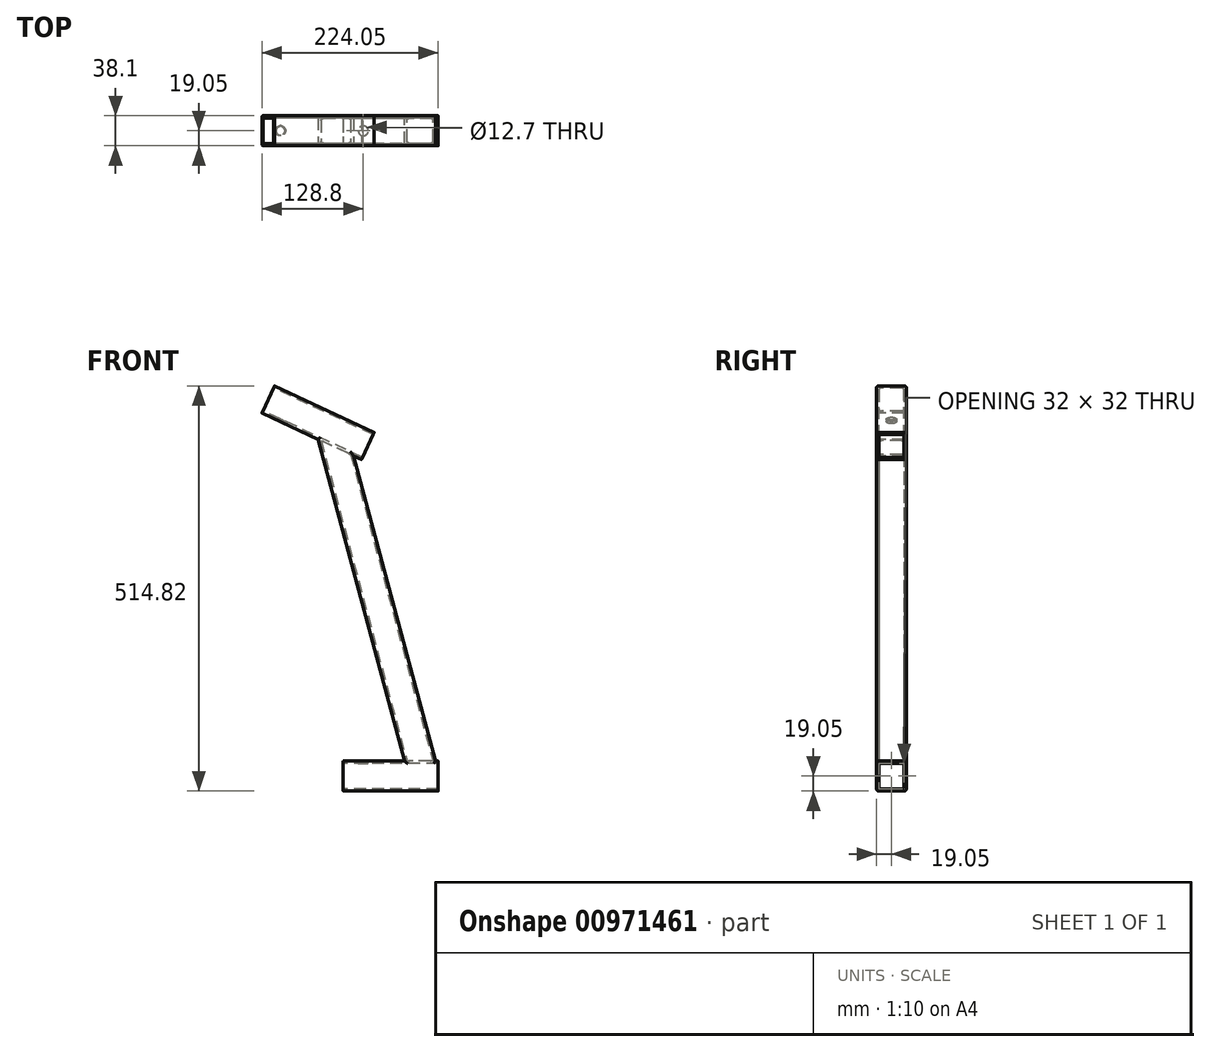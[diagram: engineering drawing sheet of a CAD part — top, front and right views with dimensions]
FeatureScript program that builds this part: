
annotation { "Feature Type Name" : "Feature", "Feature Type Description" : "" }
export const myFeature = defineFeature(function(context is Context, id is Id, definition is map)
    precondition{}
    {
        {
            var Q0;
            Q0=qCreatedBy(makeId("Right.planeOp"),FACE);
            var sketch = newSketch(context, id + "F0", { "sketchPlane" : qUnion([Q0])});
            skLineSegment(sketch, "E0.bottom", {"start": v(15.88, 19.05) * mm, "end": v(-15.88, 19.05) * mm});
            skLineSegment(sketch, "E0.top", {"start": v(15.88, -19.05) * mm, "end": v(-15.87, -19.05) * mm});
            skLineSegment(sketch, "E0.left", {"start": v(19.05, 15.88) * mm, "end": v(19.05, -15.88) * mm});
            skLineSegment(sketch, "E0.right", {"start": v(-19.05, 15.88) * mm, "end": v(-19.05, -15.88) * mm});
            skPoint(sketch, "E0.middle", {"position": v(0, 0) * mm});
            skLineSegment(sketch, "E1.0", {"start": v(-16, 12.83) * mm, "end": v(-16, -12.83) * mm});
            skLineSegment(sketch, "E1.1", {"start": v(12.83, 16) * mm, "end": v(-12.83, 16) * mm});
            skLineSegment(sketch, "E1.2", {"start": v(16, 12.83) * mm, "end": v(16, -12.83) * mm});
            skLineSegment(sketch, "E1.3", {"start": v(12.83, -16) * mm, "end": v(-12.83, -16) * mm});
            skPoint(sketch, "E2.visualSharp", {"position": v(-16, 16) * mm});
            skArc(sketch, "E2.filletArc", {"start": v(-12.83, 16) * mm, "mid": v(-15.07, 15.07) * mm, "end": v(-16, 12.83) * mm});
            skPoint(sketch, "E3.visualSharp", {"position": v(-19.05, 19.05) * mm});
            skArc(sketch, "E3.filletArc", {"start": v(-15.88, 19.05) * mm, "mid": v(-18.12, 18.12) * mm, "end": v(-19.05, 15.88) * mm});
            skPoint(sketch, "E4.visualSharp", {"position": v(19.05, 19.05) * mm});
            skArc(sketch, "E4.filletArc", {"start": v(19.05, 15.88) * mm, "mid": v(18.12, 18.12) * mm, "end": v(15.88, 19.05) * mm});
            skPoint(sketch, "E5.visualSharp", {"position": v(16, 16) * mm});
            skArc(sketch, "E5.filletArc", {"start": v(16, 12.83) * mm, "mid": v(15.07, 15.07) * mm, "end": v(12.83, 16) * mm});
            skPoint(sketch, "E6.visualSharp", {"position": v(16, -16) * mm});
            skArc(sketch, "E6.filletArc", {"start": v(12.83, -16) * mm, "mid": v(15.07, -15.07) * mm, "end": v(16, -12.83) * mm});
            skPoint(sketch, "E7.visualSharp", {"position": v(-16, -16) * mm});
            skArc(sketch, "E7.filletArc", {"start": v(-16, -12.83) * mm, "mid": v(-15.07, -15.07) * mm, "end": v(-12.83, -16) * mm});
            skPoint(sketch, "E8.visualSharp", {"position": v(-19.05, -19.05) * mm});
            skArc(sketch, "E8.filletArc", {"start": v(-19.05, -15.88) * mm, "mid": v(-18.12, -18.12) * mm, "end": v(-15.87, -19.05) * mm});
            skPoint(sketch, "E9.visualSharp", {"position": v(19.05, -19.05) * mm});
            skArc(sketch, "E9.filletArc", {"start": v(15.88, -19.05) * mm, "mid": v(18.12, -18.12) * mm, "end": v(19.05, -15.88) * mm});
            skSolve(sketch);
        }
        {
            var Q0;
            Q0 = qSketchRegion(id + "F0", true);
            extrude(context, id + "F1", {"entities" : qUnion([Q0]), "depth" : 44.45 * mm, "offsetDistance" : 25.4 * mm, "hasSecondDirection" : true, "secondDirectionOppositeDirection" : true, "secondDirectionDepth" : 76.2 * mm});
        }
        {
            var Q0;
            Q0=makeQuery(id+"F1.opExtrude","CAP_EDGE",EDGE,{"disambiguationData":[OSD([sQuery(id+"F0.wireOp",EDGE,"E0.bottom")])],"isStart":false});
            cPlane(context, id + "F2", {"entities" : qUnion([Q0]), "cplaneType" : CPlaneType.LINE_ANGLE, "offset" : 25.4 * mm, "angle" : 15 * degree, "width" : 152.4 * mm, "height" : 152.4 * mm});
        }
        {
            var Q0;
            Q0=qCreatedBy(id+"F2.planeOp",FACE);
            cPlane(context, id + "F3", {"entities" : qUnion([Q0]), "cplaneType" : CPlaneType.OFFSET, "offset" : 25.4 * mm, "oppositeDirection" : true, "width" : 152.4 * mm, "height" : 152.4 * mm});
        }
        {
            var Q0;
            Q0=qCreatedBy(id+"F3.planeOp",FACE);
            var sketch = newSketch(context, id + "F4", { "sketchPlane" : qUnion([Q0])});
            skLineSegment(sketch, "E10.bottom", {"start": v(41.28, 19.05) * mm, "end": v(9.52, 19.05) * mm});
            skLineSegment(sketch, "E10.top", {"start": v(41.28, -19.05) * mm, "end": v(9.52, -19.05) * mm});
            skLineSegment(sketch, "E10.left", {"start": v(44.45, 15.88) * mm, "end": v(44.45, -15.87) * mm});
            skLineSegment(sketch, "E10.right", {"start": v(6.35, 15.87) * mm, "end": v(6.35, -15.88) * mm});
            skPoint(sketch, "E10.middle", {"position": v(25.4, 0) * mm});
            skLineSegment(sketch, "E11.0", {"start": v(38.23, 16) * mm, "end": v(12.57, 16) * mm});
            skLineSegment(sketch, "E11.1", {"start": v(41.4, 12.83) * mm, "end": v(41.4, -12.83) * mm});
            skLineSegment(sketch, "E11.2", {"start": v(38.23, -16) * mm, "end": v(12.57, -16) * mm});
            skLineSegment(sketch, "E11.3", {"start": v(9.4, 12.83) * mm, "end": v(9.4, -12.83) * mm});
            skPoint(sketch, "E12.visualSharp", {"position": v(9.4, 16) * mm});
            skArc(sketch, "E12.filletArc", {"start": v(12.57, 16) * mm, "mid": v(10.33, 15.07) * mm, "end": v(9.4, 12.83) * mm});
            skPoint(sketch, "E13.visualSharp", {"position": v(6.35, 19.05) * mm});
            skArc(sketch, "E13.filletArc", {"start": v(9.52, 19.05) * mm, "mid": v(7.28, 18.12) * mm, "end": v(6.35, 15.87) * mm});
            skPoint(sketch, "E14.visualSharp", {"position": v(41.4, 16) * mm});
            skArc(sketch, "E14.filletArc", {"start": v(41.4, 12.83) * mm, "mid": v(40.47, 15.07) * mm, "end": v(38.23, 16) * mm});
            skPoint(sketch, "E15.visualSharp", {"position": v(44.45, 19.05) * mm});
            skArc(sketch, "E15.filletArc", {"start": v(44.45, 15.88) * mm, "mid": v(43.52, 18.12) * mm, "end": v(41.28, 19.05) * mm});
            skPoint(sketch, "E16.visualSharp", {"position": v(44.45, -19.05) * mm});
            skArc(sketch, "E16.filletArc", {"start": v(41.28, -19.05) * mm, "mid": v(43.52, -18.12) * mm, "end": v(44.45, -15.87) * mm});
            skPoint(sketch, "E17.visualSharp", {"position": v(41.4, -16) * mm});
            skArc(sketch, "E17.filletArc", {"start": v(38.23, -16) * mm, "mid": v(40.47, -15.07) * mm, "end": v(41.4, -12.83) * mm});
            skPoint(sketch, "E18.visualSharp", {"position": v(9.4, -16) * mm});
            skArc(sketch, "E18.filletArc", {"start": v(9.4, -12.83) * mm, "mid": v(10.33, -15.07) * mm, "end": v(12.57, -16) * mm});
            skPoint(sketch, "E19.visualSharp", {"position": v(6.35, -19.05) * mm});
            skArc(sketch, "E19.filletArc", {"start": v(6.35, -15.88) * mm, "mid": v(7.28, -18.12) * mm, "end": v(9.52, -19.05) * mm});
            skSolve(sketch);
        }
        {
            var Q0;
            Q0 = qSketchRegion(id + "F4", true);
            extrude(context, id + "F5", {"entities" : qUnion([Q0]), "operationType" : NewBodyOperationType.ADD, "oppositeDirection" : true, "depth" : 419.1 * mm, "offsetDistance" : 25.4 * mm, "hasSecondDirection" : true, "secondDirectionOppositeDirection" : false, "secondDirectionDepth" : 28.96 * mm});
        }
        {
            var Q0;
            Q0=makeQuery(id+"F1.opExtrude","CAP_FACE",FACE,{"disambiguationData":[OSD([sQuery(id+"F0.wireOp",EDGE,"E0.bottom"),sQuery(id+"F0.wireOp",EDGE,"E0.top"),sQuery(id+"F0.wireOp",EDGE,"E0.left"),sQuery(id+"F0.wireOp",EDGE,"E0.right"),sQuery(id+"F0.wireOp",EDGE,"E1.0"),sQuery(id+"F0.wireOp",EDGE,"E1.1"),sQuery(id+"F0.wireOp",EDGE,"E1.2"),sQuery(id+"F0.wireOp",EDGE,"E1.3"),sQuery(id+"F0.wireOp",EDGE,"E2.filletArc"),sQuery(id+"F0.wireOp",EDGE,"E3.filletArc"),sQuery(id+"F0.wireOp",EDGE,"E4.filletArc"),sQuery(id+"F0.wireOp",EDGE,"E5.filletArc"),sQuery(id+"F0.wireOp",EDGE,"E6.filletArc"),sQuery(id+"F0.wireOp",EDGE,"E7.filletArc"),sQuery(id+"F0.wireOp",EDGE,"E8.filletArc"),sQuery(id+"F0.wireOp",EDGE,"E9.filletArc")])],"isStart":true});
            var sketch = newSketch(context, id + "F6", { "sketchPlane" : qUnion([Q0])});
            skLineSegment(sketch, "E20.0", {"start": v(-12.83, 16) * mm, "end": v(12.83, 16) * mm});
            skArc(sketch, "E21.0", {"start": v(-16, 12.83) * mm, "mid": v(-15.07, 15.07) * mm, "end": v(-12.83, 16) * mm});
            skLineSegment(sketch, "E22.0", {"start": v(-16, 12.83) * mm, "end": v(-16, -12.83) * mm});
            skArc(sketch, "E23.0", {"start": v(-12.83, -16) * mm, "mid": v(-15.07, -15.07) * mm, "end": v(-16, -12.83) * mm});
            skLineSegment(sketch, "E24.0", {"start": v(-12.83, -16) * mm, "end": v(12.83, -16) * mm});
            skArc(sketch, "E25.0", {"start": v(16, -12.83) * mm, "mid": v(15.07, -15.07) * mm, "end": v(12.83, -16) * mm});
            skLineSegment(sketch, "E26.0", {"start": v(16, 12.83) * mm, "end": v(16, -12.83) * mm});
            skArc(sketch, "E27.0", {"start": v(12.83, 16) * mm, "mid": v(15.07, 15.07) * mm, "end": v(16, 12.83) * mm});
            skSolve(sketch);
        }
        {
            var Q0;
            Q0 = qSketchRegion(id + "F6", true);
            extrude(context, id + "F7", {"entities" : qUnion([Q0]), "operationType" : NewBodyOperationType.REMOVE, "oppositeDirection" : true, "depth" : 145.29 * mm, "offsetDistance" : 25.4 * mm});
        }
        {
            var Q0;
            Q0=makeQuery(id+"F5.opExtrude","CAP_EDGE",EDGE,{"disambiguationData":[OSD([sQuery(id+"F4.wireOp",EDGE,"E10.left")])],"isStart":false});
            cPlane(context, id + "F8", {"entities" : qUnion([Q0]), "cplaneType" : CPlaneType.LINE_ANGLE, "offset" : 25.4 * mm, "angle" : 115 * degree, "width" : 152.4 * mm, "height" : 152.4 * mm});
        }
        {
            var Q0;
            Q0=qCreatedBy(id+"F8.planeOp",FACE);
            var sketch = newSketch(context, id + "F9", { "sketchPlane" : qUnion([Q0])});
            skLineSegment(sketch, "E28.bottom", {"start": v(15.87, 380.23) * mm, "end": v(-15.88, 380.23) * mm});
            skLineSegment(sketch, "E28.top", {"start": v(15.87, 342.13) * mm, "end": v(-15.88, 342.13) * mm});
            skLineSegment(sketch, "E28.left", {"start": v(19.05, 377.05) * mm, "end": v(19.05, 345.3) * mm});
            skLineSegment(sketch, "E28.right", {"start": v(-19.05, 377.05) * mm, "end": v(-19.05, 345.3) * mm});
            skPoint(sketch, "E28.middle", {"position": v(0, 361.18) * mm});
            skPoint(sketch, "E28.middle.positionSnap0", {"position": v(0, 342.13) * mm});
            skPoint(sketch, "E28.centerSnap0", {"position": v(0, 345.18) * mm});
            skLineSegment(sketch, "E29.0", {"start": v(12.83, 377.18) * mm, "end": v(-12.83, 377.18) * mm});
            skLineSegment(sketch, "E29.1", {"start": v(16, 374) * mm, "end": v(16, 348.35) * mm});
            skLineSegment(sketch, "E29.2", {"start": v(12.83, 345.18) * mm, "end": v(-12.83, 345.18) * mm});
            skLineSegment(sketch, "E29.3", {"start": v(-16, 374) * mm, "end": v(-16, 348.35) * mm});
            skPoint(sketch, "E30.visualSharp", {"position": v(-19.05, 380.23) * mm});
            skArc(sketch, "E30.filletArc", {"start": v(-15.88, 380.23) * mm, "mid": v(-18.12, 379.3) * mm, "end": v(-19.05, 377.05) * mm});
            skPoint(sketch, "E31.visualSharp", {"position": v(-16, 377.18) * mm});
            skArc(sketch, "E31.filletArc", {"start": v(-12.83, 377.18) * mm, "mid": v(-15.07, 376.25) * mm, "end": v(-16, 374) * mm});
            skPoint(sketch, "E32.visualSharp", {"position": v(16, 377.18) * mm});
            skArc(sketch, "E32.filletArc", {"start": v(16, 374) * mm, "mid": v(15.07, 376.25) * mm, "end": v(12.83, 377.18) * mm});
            skPoint(sketch, "E33.visualSharp", {"position": v(19.05, 380.23) * mm});
            skArc(sketch, "E33.filletArc", {"start": v(19.05, 377.05) * mm, "mid": v(18.12, 379.3) * mm, "end": v(15.87, 380.23) * mm});
            skPoint(sketch, "E34.visualSharp", {"position": v(16, 345.18) * mm});
            skArc(sketch, "E34.filletArc", {"start": v(12.83, 345.18) * mm, "mid": v(15.07, 346.1) * mm, "end": v(16, 348.35) * mm});
            skPoint(sketch, "E35.visualSharp", {"position": v(19.05, 342.13) * mm});
            skArc(sketch, "E35.filletArc", {"start": v(15.87, 342.13) * mm, "mid": v(18.12, 343.06) * mm, "end": v(19.05, 345.3) * mm});
            skPoint(sketch, "E36.visualSharp", {"position": v(-19.05, 342.13) * mm});
            skArc(sketch, "E36.filletArc", {"start": v(-19.05, 345.3) * mm, "mid": v(-18.12, 343.06) * mm, "end": v(-15.88, 342.13) * mm});
            skPoint(sketch, "E37.visualSharp", {"position": v(-16, 345.18) * mm});
            skArc(sketch, "E37.filletArc", {"start": v(-16, 348.35) * mm, "mid": v(-15.07, 346.1) * mm, "end": v(-12.83, 345.18) * mm});
            skSolve(sketch);
        }
        {
            var Q0;
            Q0 = qSketchRegion(id + "F9", true);
            extrude(context, id + "F10", {"entities" : qUnion([Q0]), "operationType" : NewBodyOperationType.ADD, "depth" : 38.1 * mm, "offsetDistance" : 25.4 * mm, "hasSecondDirection" : true, "secondDirectionOppositeDirection" : true, "secondDirectionDepth" : 101.6 * mm});
        }
        {
            var Q0;
            Q0=makeQuery(id+"F10.opExtrude","CAP_FACE",FACE,{"disambiguationData":[OSD([sQuery(id+"F9.wireOp",EDGE,"E28.bottom"),sQuery(id+"F9.wireOp",EDGE,"E28.top"),sQuery(id+"F9.wireOp",EDGE,"E28.left"),sQuery(id+"F9.wireOp",EDGE,"E28.right"),sQuery(id+"F9.wireOp",EDGE,"E29.0"),sQuery(id+"F9.wireOp",EDGE,"E29.1"),sQuery(id+"F9.wireOp",EDGE,"E29.2"),sQuery(id+"F9.wireOp",EDGE,"E29.3"),sQuery(id+"F9.wireOp",EDGE,"E30.filletArc"),sQuery(id+"F9.wireOp",EDGE,"E31.filletArc"),sQuery(id+"F9.wireOp",EDGE,"E32.filletArc"),sQuery(id+"F9.wireOp",EDGE,"E33.filletArc"),sQuery(id+"F9.wireOp",EDGE,"E34.filletArc"),sQuery(id+"F9.wireOp",EDGE,"E35.filletArc"),sQuery(id+"F9.wireOp",EDGE,"E36.filletArc"),sQuery(id+"F9.wireOp",EDGE,"E37.filletArc")])],"isStart":false});
            var sketch = newSketch(context, id + "F11", { "sketchPlane" : qUnion([Q0])});
            skLineSegment(sketch, "E38.0", {"start": v(-16, 374) * mm, "end": v(-16, 348.35) * mm});
            skArc(sketch, "E39.0", {"start": v(-12.83, 377.18) * mm, "mid": v(-15.07, 376.25) * mm, "end": v(-16, 374) * mm});
            skLineSegment(sketch, "E40.0", {"start": v(12.83, 377.18) * mm, "end": v(-12.83, 377.18) * mm});
            skArc(sketch, "E41.0", {"start": v(16, 374) * mm, "mid": v(15.07, 376.25) * mm, "end": v(12.83, 377.18) * mm});
            skLineSegment(sketch, "E42.0", {"start": v(16, 374) * mm, "end": v(16, 348.35) * mm});
            skArc(sketch, "E43.0", {"start": v(12.83, 345.18) * mm, "mid": v(15.07, 346.1) * mm, "end": v(16, 348.35) * mm});
            skLineSegment(sketch, "E44.0", {"start": v(12.83, 345.18) * mm, "end": v(-12.83, 345.18) * mm});
            skArc(sketch, "E45.0", {"start": v(-16, 348.35) * mm, "mid": v(-15.07, 346.1) * mm, "end": v(-12.83, 345.18) * mm});
            skSolve(sketch);
        }
        {
            var Q0;
            Q0 = qSketchRegion(id + "F11", true);
            extrude(context, id + "F12", {"entities" : qUnion([Q0]), "operationType" : NewBodyOperationType.REMOVE, "endBound" : BoundingType.THROUGH_ALL, "oppositeDirection" : true, "depth" : 25.4 * mm, "offsetDistance" : 25.4 * mm});
        }
        {
            var Q0;
            {var subQ2=sQuery(id+"F0.wireOp",EDGE,"E0.bottom");Q0=makeQuery(id+"F5.boolean.opBoolean","SPLIT",FACE,{"disambiguationData":[TD([makeQuery(id+"F5.opExtrude","SWEPT_FACE",FACE,{"disambiguationData":[OSD([sQuery(id+"F4.wireOp",EDGE,"E10.right")])]})])],"derivedFrom":makeQuery(id+"F1.opExtrude","SWEPT_FACE",FACE,{"disambiguationData":[OSD([subQ2])]})});}
            var sketch = newSketch(context, id + "F13", { "sketchPlane" : qUnion([Q0])});
            skCircle(sketch, "E46", {"center": v(-50.8, 0) * mm, "radius": 6.35 * mm});
            skSolve(sketch);
        }
        {
            var Q0;
            Q0 = qSketchRegion(id + "F13", true);
            extrude(context, id + "F14", {"entities" : qUnion([Q0]), "operationType" : NewBodyOperationType.REMOVE, "oppositeDirection" : true, "depth" : 6.35 * mm, "offsetDistance" : 25.4 * mm});
        }
        {
            var Q0;
            {var subQ2=sQuery(id+"F9.wireOp",EDGE,"E28.top");Q0=makeQuery(id+"F10.boolean.opBoolean","SPLIT",FACE,{"disambiguationData":[TD([makeQuery(id+"F5.opExtrude","SWEPT_FACE",FACE,{"disambiguationData":[OSD([sQuery(id+"F4.wireOp",EDGE,"E10.right")])]})])],"derivedFrom":makeQuery(id+"F10.opExtrude","SWEPT_FACE",FACE,{"disambiguationData":[OSD([subQ2])]})});}
            var sketch = newSketch(context, id + "F15", { "sketchPlane" : qUnion([Q0])});
            skCircle(sketch, "E47", {"center": v(-332.3, 0) * mm, "radius": 6.35 * mm});
            skSolve(sketch);
        }
        {
            var Q0;
            Q0 = qSketchRegion(id + "F15", true);
            extrude(context, id + "F16", {"entities" : qUnion([Q0]), "operationType" : NewBodyOperationType.REMOVE, "oppositeDirection" : true, "depth" : 6.35 * mm, "offsetDistance" : 25.4 * mm});
        }
    });
